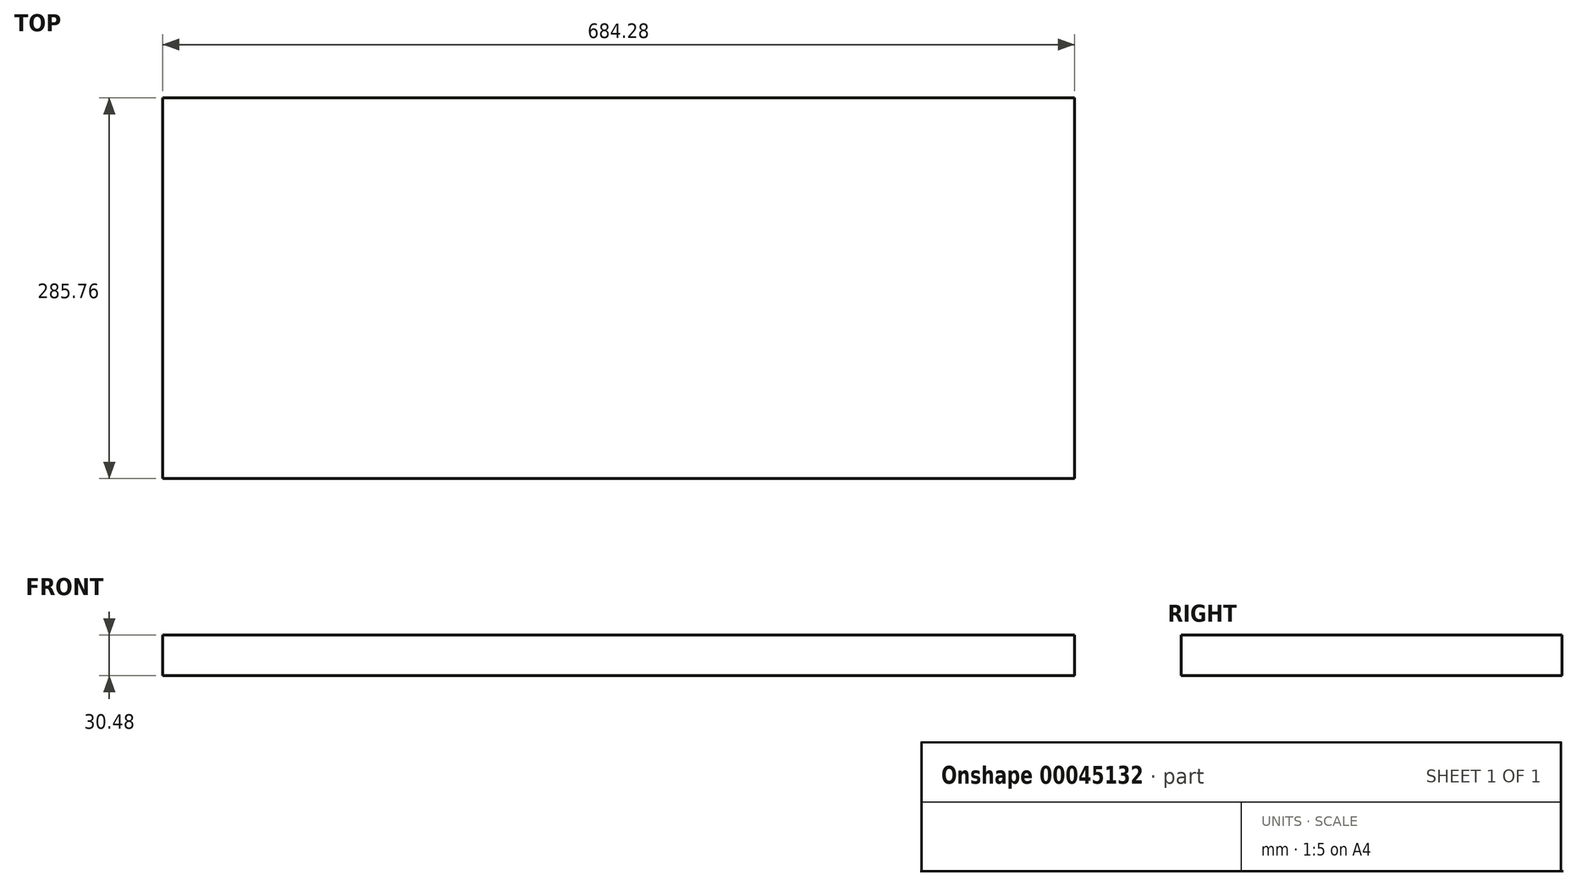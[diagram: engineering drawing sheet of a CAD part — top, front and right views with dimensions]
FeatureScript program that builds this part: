
annotation { "Feature Type Name" : "Feature", "Feature Type Description" : "" }
export const myFeature = defineFeature(function(context is Context, id is Id, definition is map)
    precondition{}
    {
        {
            var Q0;
            Q0=qCreatedBy(makeId("Top.planeOp"),FACE);
            var sketch = newSketch(context, id + "F0", { "sketchPlane" : qUnion([Q0])});
            skLineSegment(sketch, "E0.rect.bottom", {"start": v(342.14, -142.87) * mm, "end": v(-342.14, -142.88) * mm});
            skPoint(sketch, "E0.rect.middle", {"position": v(0, 0) * mm});
            skLineSegment(sketch, "E1", {"start": v(-318.66, 142.88) * mm, "end": v(342.14, 142.88) * mm});
            skLineSegment(sketch, "E2", {"start": v(-342.14, -142.88) * mm, "end": v(-342.14, 142.88) * mm});
            skLineSegment(sketch, "E3", {"start": v(-342.14, 142.88) * mm, "end": v(-318.66, 142.88) * mm});
            skLineSegment(sketch, "E4", {"start": v(342.14, 142.88) * mm, "end": v(342.14, -142.87) * mm});
            skSolve(sketch);
        }
        {
            var Q0;
            Q0=makeQuery(id+"F0.imprint","IMPRINT",FACE,{"disambiguationData":[TD([[makeQuery(id+"F0.imprint","IMPRINT",EDGE,{"derivedFrom":sQuery(id+"F0.wireOp",EDGE,"E0.rect.bottom")}),-1.0]])]});
            extrude(context, id + "F1", {"entities" : qUnion([Q0]), "depth" : 30.48 * mm});
        }
    });
